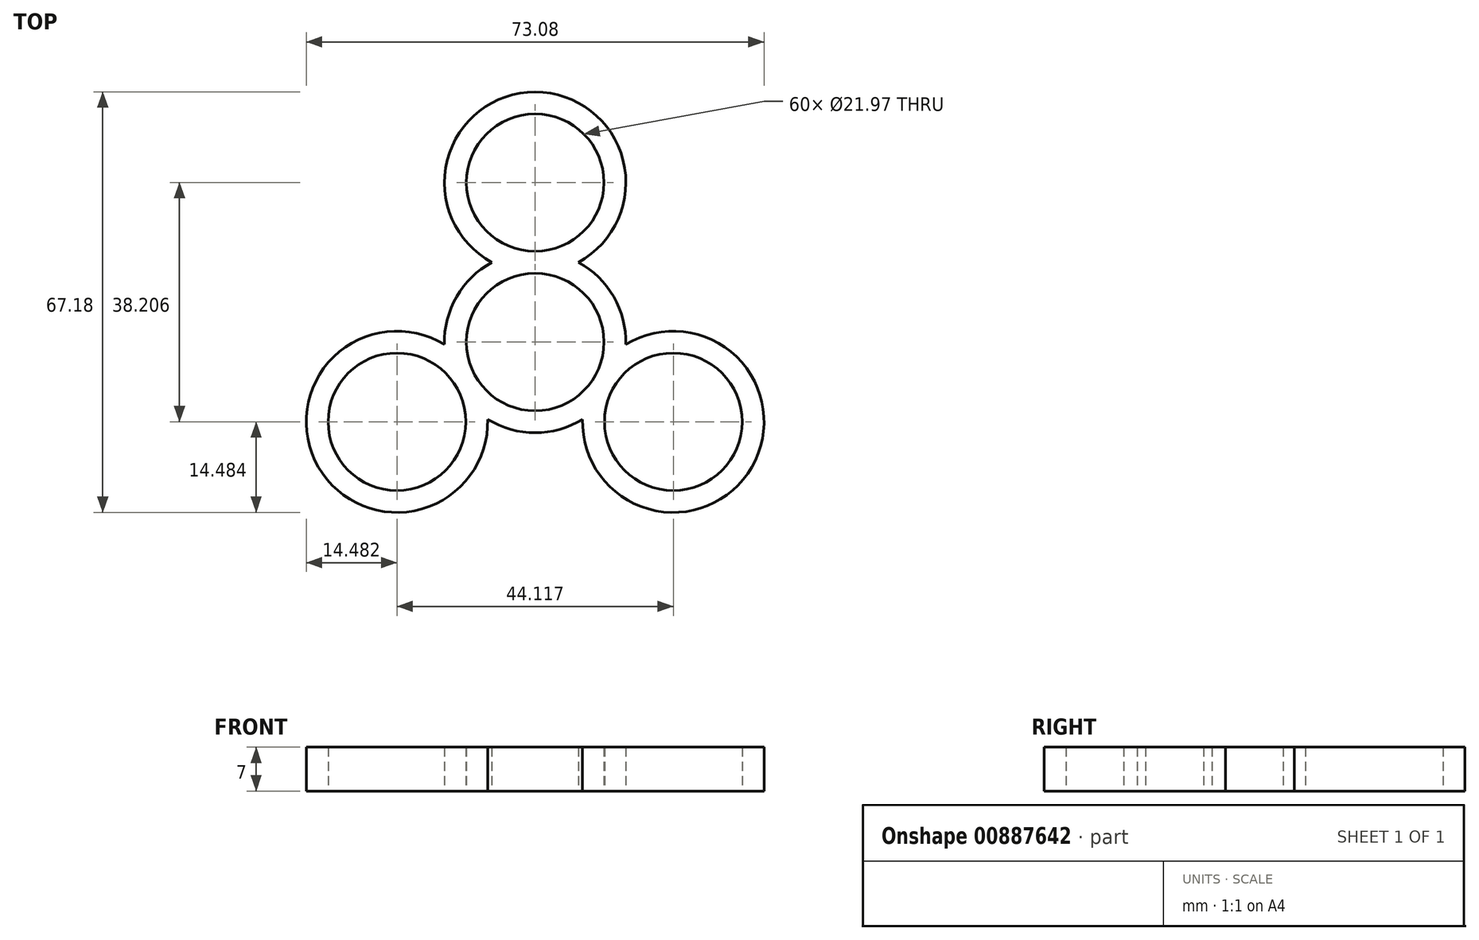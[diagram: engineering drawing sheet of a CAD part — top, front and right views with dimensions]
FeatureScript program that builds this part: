
annotation { "Feature Type Name" : "Feature", "Feature Type Description" : "" }
export const myFeature = defineFeature(function(context is Context, id is Id, definition is map)
    precondition{}
    {
        {
            var Q0;
            Q0=qCreatedBy(makeId("Top.planeOp"),FACE);
            var sketch = newSketch(context, id + "F0", { "sketchPlane" : qUnion([Q0])});
            skCircle(sketch, "E0", {"center": v(0, 0) * mm, "radius": 10.99 * mm});
            skCircle(sketch, "E1", {"center": v(0, 0) * mm, "radius": 25.47 * mm, "construction": true});
            skCircle(sketch, "E2", {"center": v(0, 25.47) * mm, "radius": 10.99 * mm});
            skCircle(sketch, "E3", {"center": v(-22.06, -12.74) * mm, "radius": 10.99 * mm});
            skCircle(sketch, "E4", {"center": v(22.06, -12.74) * mm, "radius": 10.99 * mm});
            skLineSegment(sketch, "E5", {"start": v(-22.06, -12.74) * mm, "end": v(22.06, -12.74) * mm, "construction": true});
            skLineSegment(sketch, "E6", {"start": v(0, 25.47) * mm, "end": v(-22.06, -12.74) * mm, "construction": true});
            skLineSegment(sketch, "E7", {"start": v(22.06, -12.74) * mm, "end": v(0, 25.47) * mm, "construction": true});
            skLineSegment(sketch, "E8.bottom", {"start": v(-57.15, 57.15) * mm, "end": v(57.15, 57.15) * mm, "construction": true});
            skLineSegment(sketch, "E8.top", {"start": v(-57.15, -57.15) * mm, "end": v(57.15, -57.15) * mm, "construction": true});
            skLineSegment(sketch, "E8.left", {"start": v(-57.15, 57.15) * mm, "end": v(-57.15, -57.15) * mm, "construction": true});
            skLineSegment(sketch, "E8.right", {"start": v(57.15, 57.15) * mm, "end": v(57.15, -57.15) * mm, "construction": true});
            skPoint(sketch, "E9", {"position": v(-57.15, 0) * mm});
            skPoint(sketch, "E10", {"position": v(0, 57.15) * mm});
            skSolve(sketch);
        }
        {
            var Q0;
            Q0=qCreatedBy(makeId("Top.planeOp"),FACE);
            var sketch = newSketch(context, id + "F1", { "sketchPlane" : qUnion([Q0])});
            skCircle(sketch, "E11", {"center": v(0, 0) * mm, "radius": 10.99 * mm});
            skCircle(sketch, "E12", {"center": v(-22.06, -12.74) * mm, "radius": 10.99 * mm});
            skCircle(sketch, "E13", {"center": v(0, 25.47) * mm, "radius": 10.99 * mm});
            skCircle(sketch, "E14", {"center": v(22.06, -12.74) * mm, "radius": 10.99 * mm});
            skLineSegment(sketch, "E15.bottom", {"start": v(-57.15, 57.15) * mm, "end": v(57.15, 57.15) * mm, "construction": true});
            skLineSegment(sketch, "E15.top", {"start": v(-57.15, -57.15) * mm, "end": v(57.15, -57.15) * mm, "construction": true});
            skLineSegment(sketch, "E15.left", {"start": v(-57.15, 57.15) * mm, "end": v(-57.15, -57.15) * mm, "construction": true});
            skLineSegment(sketch, "E15.right", {"start": v(57.15, 57.15) * mm, "end": v(57.15, -57.15) * mm, "construction": true});
            skPoint(sketch, "E16", {"position": v(-57.15, 0) * mm});
            skPoint(sketch, "E17", {"position": v(0, 57.15) * mm});
            skArc(sketch, "E18", {"start": v(-15.16, 0) * mm, "mid": v(-34.4, -20.31) * mm, "end": v(-7.58, -12.35) * mm});
            skArc(sketch, "E19", {"start": v(6.9, 12.74) * mm, "mid": v(0, 39.96) * mm, "end": v(-6.9, 12.74) * mm});
            skArc(sketch, "E20", {"start": v(7.58, -12.35) * mm, "mid": v(34.6, -19.98) * mm, "end": v(14.48, -0.4) * mm});
            skArc(sketch, "E21", {"start": v(-6.9, 12.74) * mm, "mid": v(-12.54, 7.24) * mm, "end": v(-14.48, -0.4) * mm});
            skArc(sketch, "E22", {"start": v(-14.48, -0.4) * mm, "mid": v(-14.82, -0.2) * mm, "end": v(-15.16, 0) * mm});
            skArc(sketch, "E23.trimOffspring", {"start": v(14.48, -0.4) * mm, "mid": v(12.54, 7.24) * mm, "end": v(6.9, 12.74) * mm});
            skArc(sketch, "E24.trimOffspring", {"start": v(-7.58, -12.35) * mm, "mid": v(0, -14.49) * mm, "end": v(7.58, -12.35) * mm});
            skSolve(sketch);
        }
        {
            var Q0;
            Q0 = qSketchRegion(id + "F1", true);
            extrude(context, id + "F2", {"entities" : qUnion([Q0]), "depth" : 7 * mm, "offsetDistance" : 25.4 * mm});
        }
    });
